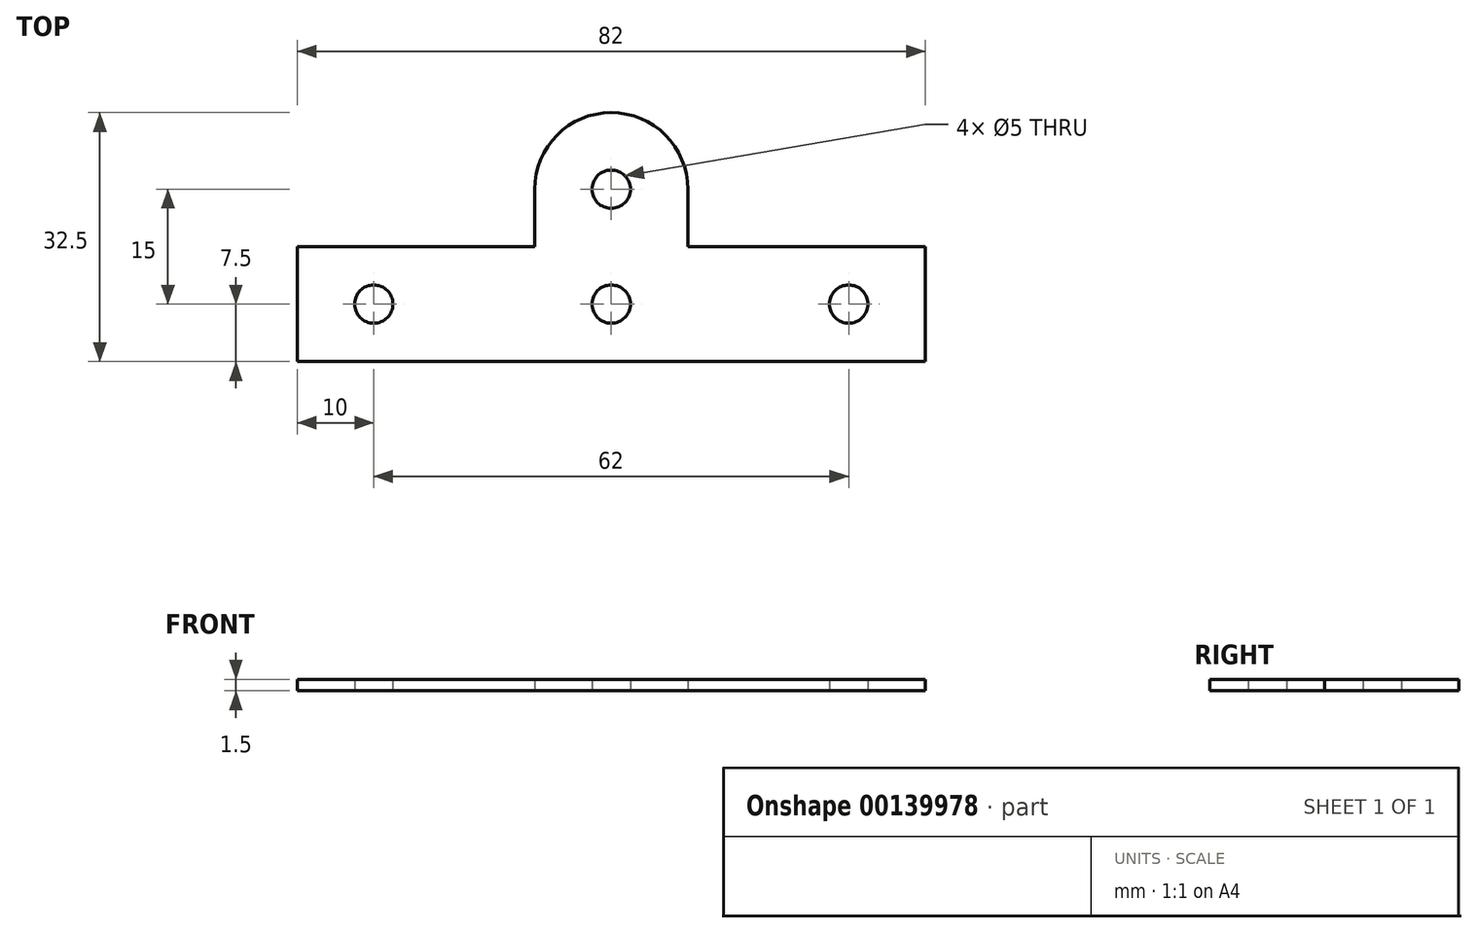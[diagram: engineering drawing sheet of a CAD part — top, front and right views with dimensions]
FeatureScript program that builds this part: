
annotation { "Feature Type Name" : "Feature", "Feature Type Description" : "" }
export const myFeature = defineFeature(function(context is Context, id is Id, definition is map)
    precondition{}
    {
        {
            var Q0;
            Q0=qCreatedBy(makeId("Top.planeOp"),FACE);
            var sketch = newSketch(context, id + "F0", { "sketchPlane" : qUnion([Q0])});
            skCircle(sketch, "E0", {"center": v(0, 0) * mm, "radius": 2.5 * mm});
            skLineSegment(sketch, "E1", {"start": v(-41, 0) * mm, "end": v(41, 0) * mm, "construction": true});
            skLineSegment(sketch, "E2", {"start": v(-41, 7.5) * mm, "end": v(-41, -7.5) * mm});
            skLineSegment(sketch, "E3", {"start": v(41, 7.5) * mm, "end": v(41, -7.5) * mm});
            skLineSegment(sketch, "E4", {"start": v(-41, -7.5) * mm, "end": v(41, -7.5) * mm});
            skLineSegment(sketch, "E5", {"start": v(-41, 7.5) * mm, "end": v(-10, 7.5) * mm});
            skPoint(sketch, "E6", {"position": v(31, 0) * mm});
            skPoint(sketch, "E7", {"position": v(-31, 0) * mm});
            skCircle(sketch, "E8", {"center": v(-31, 0) * mm, "radius": 2.5 * mm});
            skCircle(sketch, "E9", {"center": v(31, 0) * mm, "radius": 2.5 * mm});
            skPoint(sketch, "E10", {"position": v(0, 7.5) * mm});
            skPoint(sketch, "E11", {"position": v(10, 7.5) * mm});
            skPoint(sketch, "E12", {"position": v(-10, 7.5) * mm});
            skLineSegment(sketch, "E13", {"start": v(10, 7.5) * mm, "end": v(10, 15) * mm});
            skLineSegment(sketch, "E14", {"start": v(-10, 7.5) * mm, "end": v(-10, 15) * mm});
            skArc(sketch, "E15", {"start": v(-10, 15) * mm, "mid": v(0, 25) * mm, "end": v(10, 15) * mm});
            skCircle(sketch, "E16", {"center": v(0, 15) * mm, "radius": 2.5 * mm});
            skLineSegment(sketch, "E17.trimOffspring", {"start": v(10, 7.5) * mm, "end": v(41, 7.5) * mm});
            skSolve(sketch);
        }
        {
            var Q0;
            Q0 = qSketchRegion(id + "F0", true);
            extrude(context, id + "F1", {"entities" : qUnion([Q0]), "endBound" : BoundingType.SYMMETRIC, "depth" : 1.5 * mm});
        }
    });
